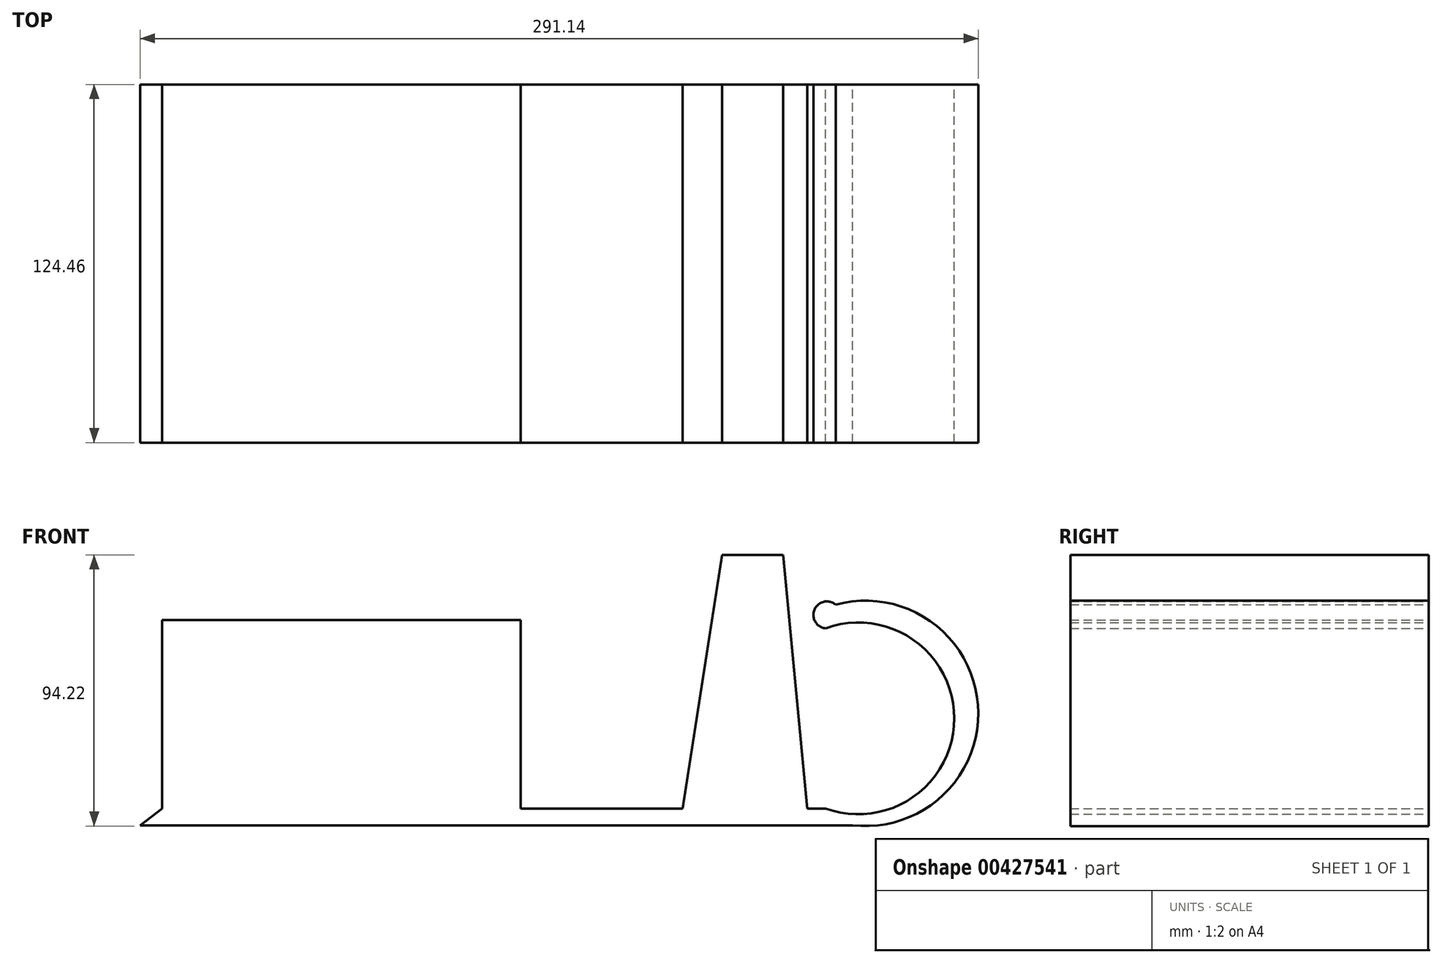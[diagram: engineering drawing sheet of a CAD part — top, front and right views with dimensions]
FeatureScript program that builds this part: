
annotation { "Feature Type Name" : "Feature", "Feature Type Description" : "" }
export const myFeature = defineFeature(function(context is Context, id is Id, definition is map)
    precondition{}
    {
        {
            var Q0;
            Q0=qCreatedBy(makeId("Front.planeOp"),FACE);
            var sketch = newSketch(context, id + "F0", { "sketchPlane" : qUnion([Q0])});
            skLineSegment(sketch, "E0.bottom", {"start": v(-102.83, 34.5) * mm, "end": v(21.79, 34.5) * mm});
            skLineSegment(sketch, "E0.top", {"start": v(-102.83, -31.02) * mm, "end": v(21.79, -31.02) * mm});
            skLineSegment(sketch, "E0.left", {"start": v(-102.83, 34.5) * mm, "end": v(-102.83, -31.02) * mm});
            skLineSegment(sketch, "E0.right", {"start": v(21.79, 34.5) * mm, "end": v(21.79, -31.02) * mm});
            skLineSegment(sketch, "E1", {"start": v(-102.83, -31.02) * mm, "end": v(127.68, -31.02) * mm});
            skLineSegment(sketch, "E2", {"start": v(127.68, -31.02) * mm, "end": v(137.04, -36.87) * mm});
            skLineSegment(sketch, "E3", {"start": v(137.04, -36.87) * mm, "end": v(-110.43, -36.87) * mm});
            skLineSegment(sketch, "E4", {"start": v(-110.43, -36.87) * mm, "end": v(-102.83, -31.02) * mm});
            skArc(sketch, "E5", {"start": v(137.04, -36.87) * mm, "mid": v(180.6, 5) * mm, "end": v(131.2, 39.77) * mm});
            skArc(sketch, "E6", {"start": v(127.68, -31.02) * mm, "mid": v(172.37, 0.28) * mm, "end": v(127.68, 31.58) * mm});
            skArc(sketch, "E7", {"start": v(131.2, 39.77) * mm, "mid": v(123.82, 38.08) * mm, "end": v(127.68, 31.58) * mm});
            skLineSegment(sketch, "E8", {"start": v(77.99, -31.02) * mm, "end": v(91.76, 57.1) * mm});
            skLineSegment(sketch, "E9", {"start": v(91.76, 57.1) * mm, "end": v(112.92, 57.1) * mm});
            skLineSegment(sketch, "E10", {"start": v(112.92, 57.1) * mm, "end": v(121.28, -31.02) * mm});
            skSolve(sketch);
        }
        {
            var Q0;
            Q0 = qSketchRegion(id + "F0", true);
            extrude(context, id + "F1", {"entities" : qUnion([Q0]), "depth" : 124.46 * mm});
        }
    });
